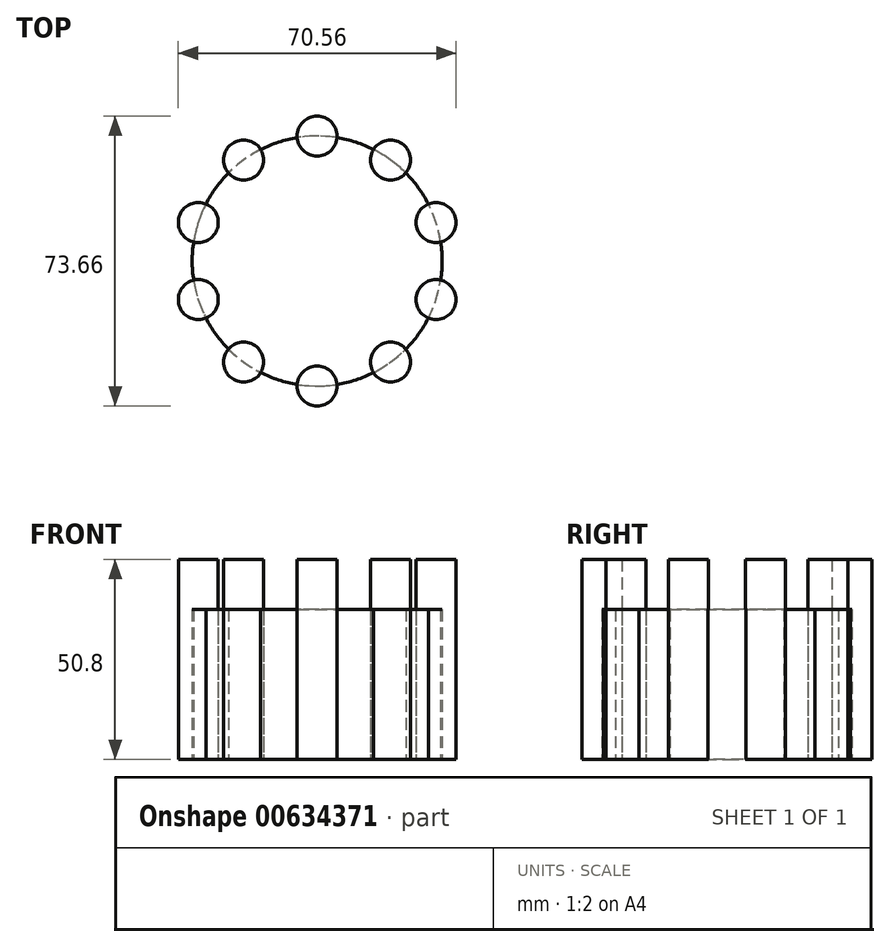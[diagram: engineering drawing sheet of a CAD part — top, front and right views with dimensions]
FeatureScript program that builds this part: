
annotation { "Feature Type Name" : "Feature", "Feature Type Description" : "" }
export const myFeature = defineFeature(function(context is Context, id is Id, definition is map)
    precondition{}
    {
        {
            var Q0;
            Q0=qCreatedBy(makeId("Top.planeOp"),FACE);
            var sketch = newSketch(context, id + "F0", { "sketchPlane" : qUnion([Q0])});
            skCircle(sketch, "E0", {"center": v(0, 0) * mm, "radius": 31.75 * mm});
            skSolve(sketch);
        }
        {
            var Q0;
            Q0=qSketchRegion(id+"F0",true);
            extrude(context, id + "F1", {"entities" : qUnion([Q0]), "depth" : 38.1 * mm});
        }
        {
            var Q0;
            Q0=qCreatedBy(makeId("Top.planeOp"),FACE);
            var sketch = newSketch(context, id + "F2", { "sketchPlane" : qUnion([Q0])});
            skCircle(sketch, "E1", {"center": v(0, 31.75) * mm, "radius": 5.08 * mm});
            skCircle(sketch, "E2.1.0", {"center": v(-18.66, 25.69) * mm, "radius": 5.08 * mm});
            skCircle(sketch, "E2.2.0", {"center": v(-30.2, 9.81) * mm, "radius": 5.08 * mm});
            skCircle(sketch, "E2.3.0", {"center": v(-30.2, -9.81) * mm, "radius": 5.08 * mm});
            skCircle(sketch, "E2.4.0", {"center": v(-18.66, -25.69) * mm, "radius": 5.08 * mm});
            skCircle(sketch, "E2.5.0", {"center": v(0, -31.75) * mm, "radius": 5.08 * mm});
            skCircle(sketch, "E2.6.0", {"center": v(18.66, -25.69) * mm, "radius": 5.08 * mm});
            skCircle(sketch, "E2.7.0", {"center": v(30.2, -9.81) * mm, "radius": 5.08 * mm});
            skCircle(sketch, "E2.8.0", {"center": v(30.2, 9.81) * mm, "radius": 5.08 * mm});
            skCircle(sketch, "E2.9.0", {"center": v(18.66, 25.69) * mm, "radius": 5.08 * mm});
            skPoint(sketch, "E2.center", {"position": v(0, 0) * mm});
            skSolve(sketch);
        }
        {
            var Q0;
            Q0=qSketchRegion(id+"F2",true);
            extrude(context, id + "F3", {"entities" : qUnion([Q0]), "depth" : 50.8 * mm});
        }
        {
            var Q0;
            Q0=makeQuery(id+"F1.opExtrude","SWEPT_BODY",BODY,{"disambiguationData":[OSD([sQuery(id+"F0.wireOp",EDGE,"E0")])]});
            var Q1;
            Q1=makeQuery(id+"F3.opExtrude","SWEPT_BODY",BODY,{"disambiguationData":[OSD([sQuery(id+"F2.wireOp",EDGE,"E1")])]});
            var Q2;
            Q2=makeQuery(id+"F3.opExtrude","SWEPT_BODY",BODY,{"disambiguationData":[OSD([sQuery(id+"F2.wireOp",EDGE,"E2.1.0")])]});
            var Q3;
            Q3=makeQuery(id+"F3.opExtrude","SWEPT_BODY",BODY,{"disambiguationData":[OSD([sQuery(id+"F2.wireOp",EDGE,"E2.2.0")])]});
            var Q4;
            Q4=makeQuery(id+"F3.opExtrude","SWEPT_BODY",BODY,{"disambiguationData":[OSD([sQuery(id+"F2.wireOp",EDGE,"E2.3.0")])]});
            var Q5;
            Q5=makeQuery(id+"F3.opExtrude","SWEPT_BODY",BODY,{"disambiguationData":[OSD([sQuery(id+"F2.wireOp",EDGE,"E2.4.0")])]});
            var Q6;
            Q6=makeQuery(id+"F3.opExtrude","SWEPT_BODY",BODY,{"disambiguationData":[OSD([sQuery(id+"F2.wireOp",EDGE,"E2.5.0")])]});
            var Q7;
            Q7=makeQuery(id+"F3.opExtrude","SWEPT_BODY",BODY,{"disambiguationData":[OSD([sQuery(id+"F2.wireOp",EDGE,"E2.6.0")])]});
            var Q8;
            Q8=makeQuery(id+"F3.opExtrude","SWEPT_BODY",BODY,{"disambiguationData":[OSD([sQuery(id+"F2.wireOp",EDGE,"E2.7.0")])]});
            var Q9;
            Q9=makeQuery(id+"F3.opExtrude","SWEPT_BODY",BODY,{"disambiguationData":[OSD([sQuery(id+"F2.wireOp",EDGE,"E2.8.0")])]});
            var Q10;
            Q10=makeQuery(id+"F3.opExtrude","SWEPT_BODY",BODY,{"disambiguationData":[OSD([sQuery(id+"F2.wireOp",EDGE,"E2.9.0")])]});
            booleanBodies(context, id + "F4", {"operationType" : BooleanOperationType.INTERSECTION, "tools" : qUnion([Q0, Q1, Q2, Q3, Q4, Q5, Q6, Q7, Q8, Q9, Q10]), "keepTools" : true});
        }
        {
            var Q0;
            Q0=makeQuery(id+"F1.opExtrude","SWEPT_BODY",BODY,{"disambiguationData":[OSD([sQuery(id+"F0.wireOp",EDGE,"E0")])]});
            var Q1;
            Q1=makeQuery(id+"F3.opExtrude","SWEPT_BODY",BODY,{"disambiguationData":[OSD([sQuery(id+"F2.wireOp",EDGE,"E2.3.0")])]});
            booleanBodies(context, id + "F5", {"operationType" : BooleanOperationType.INTERSECTION, "tools" : qUnion([Q0, Q1]), "keepTools" : true});
        }
        {
            var Q0;
            Q0=makeQuery(id+"F1.opExtrude","SWEPT_BODY",BODY,{"disambiguationData":[OSD([sQuery(id+"F0.wireOp",EDGE,"E0")])]});
            var Q1;
            Q1=makeQuery(id+"F3.opExtrude","SWEPT_BODY",BODY,{"disambiguationData":[OSD([sQuery(id+"F2.wireOp",EDGE,"E2.4.0")])]});
            booleanBodies(context, id + "F6", {"operationType" : BooleanOperationType.INTERSECTION, "tools" : qUnion([Q0, Q1]), "keepTools" : true});
        }
        {
            var Q0;
            Q0=makeQuery(id+"F1.opExtrude","SWEPT_BODY",BODY,{"disambiguationData":[OSD([sQuery(id+"F0.wireOp",EDGE,"E0")])]});
            var Q1;
            Q1=makeQuery(id+"F3.opExtrude","SWEPT_BODY",BODY,{"disambiguationData":[OSD([sQuery(id+"F2.wireOp",EDGE,"E2.5.0")])]});
            booleanBodies(context, id + "F7", {"operationType" : BooleanOperationType.INTERSECTION, "tools" : qUnion([Q0, Q1]), "keepTools" : true});
        }
        {
            var Q0;
            Q0=makeQuery(id+"F1.opExtrude","SWEPT_BODY",BODY,{"disambiguationData":[OSD([sQuery(id+"F0.wireOp",EDGE,"E0")])]});
            var Q1;
            Q1=makeQuery(id+"F3.opExtrude","SWEPT_BODY",BODY,{"disambiguationData":[OSD([sQuery(id+"F2.wireOp",EDGE,"E2.6.0")])]});
            booleanBodies(context, id + "F8", {"operationType" : BooleanOperationType.INTERSECTION, "tools" : qUnion([Q0, Q1]), "keepTools" : true});
        }
        {
            var Q0;
            Q0=makeQuery(id+"F1.opExtrude","SWEPT_BODY",BODY,{"disambiguationData":[OSD([sQuery(id+"F0.wireOp",EDGE,"E0")])]});
            var Q1;
            Q1=makeQuery(id+"F3.opExtrude","SWEPT_BODY",BODY,{"disambiguationData":[OSD([sQuery(id+"F2.wireOp",EDGE,"E2.7.0")])]});
            booleanBodies(context, id + "F9", {"operationType" : BooleanOperationType.INTERSECTION, "tools" : qUnion([Q0, Q1]), "keepTools" : true});
        }
        {
            var Q0;
            Q0=makeQuery(id+"F1.opExtrude","SWEPT_BODY",BODY,{"disambiguationData":[OSD([sQuery(id+"F0.wireOp",EDGE,"E0")])]});
            var Q1;
            Q1=makeQuery(id+"F3.opExtrude","SWEPT_BODY",BODY,{"disambiguationData":[OSD([sQuery(id+"F2.wireOp",EDGE,"E2.8.0")])]});
            booleanBodies(context, id + "F10", {"operationType" : BooleanOperationType.INTERSECTION, "tools" : qUnion([Q0, Q1]), "keepTools" : true});
        }
        {
            var Q0;
            Q0=makeQuery(id+"F1.opExtrude","SWEPT_BODY",BODY,{"disambiguationData":[OSD([sQuery(id+"F0.wireOp",EDGE,"E0")])]});
            var Q1;
            Q1=makeQuery(id+"F3.opExtrude","SWEPT_BODY",BODY,{"disambiguationData":[OSD([sQuery(id+"F2.wireOp",EDGE,"E2.9.0")])]});
            booleanBodies(context, id + "F11", {"operationType" : BooleanOperationType.INTERSECTION, "tools" : qUnion([Q0, Q1]), "keepTools" : true});
        }
        {
            var Q0;
            Q0=makeQuery(id+"F1.opExtrude","SWEPT_BODY",BODY,{"disambiguationData":[OSD([sQuery(id+"F0.wireOp",EDGE,"E0")])]});
            var Q1;
            Q1=makeQuery(id+"F3.opExtrude","SWEPT_BODY",BODY,{"disambiguationData":[OSD([sQuery(id+"F2.wireOp",EDGE,"E1")])]});
            booleanBodies(context, id + "F12", {"operationType" : BooleanOperationType.INTERSECTION, "tools" : qUnion([Q0, Q1]), "keepTools" : true});
        }
        {
            var Q0;
            Q0=makeQuery(id+"F1.opExtrude","SWEPT_BODY",BODY,{"disambiguationData":[OSD([sQuery(id+"F0.wireOp",EDGE,"E0")])]});
            var Q1;
            Q1=makeQuery(id+"F3.opExtrude","SWEPT_BODY",BODY,{"disambiguationData":[OSD([sQuery(id+"F2.wireOp",EDGE,"E2.1.0")])]});
            booleanBodies(context, id + "F13", {"operationType" : BooleanOperationType.INTERSECTION, "tools" : qUnion([Q0, Q1]), "keepTools" : true});
        }
        {
            var Q0;
            Q0=makeQuery(id+"F1.opExtrude","SWEPT_BODY",BODY,{"disambiguationData":[OSD([sQuery(id+"F0.wireOp",EDGE,"E0")])]});
            var Q1;
            Q1=makeQuery(id+"F3.opExtrude","SWEPT_BODY",BODY,{"disambiguationData":[OSD([sQuery(id+"F2.wireOp",EDGE,"E2.2.0")])]});
            booleanBodies(context, id + "F14", {"operationType" : BooleanOperationType.INTERSECTION, "tools" : qUnion([Q0, Q1]), "keepTools" : true});
        }
    });
